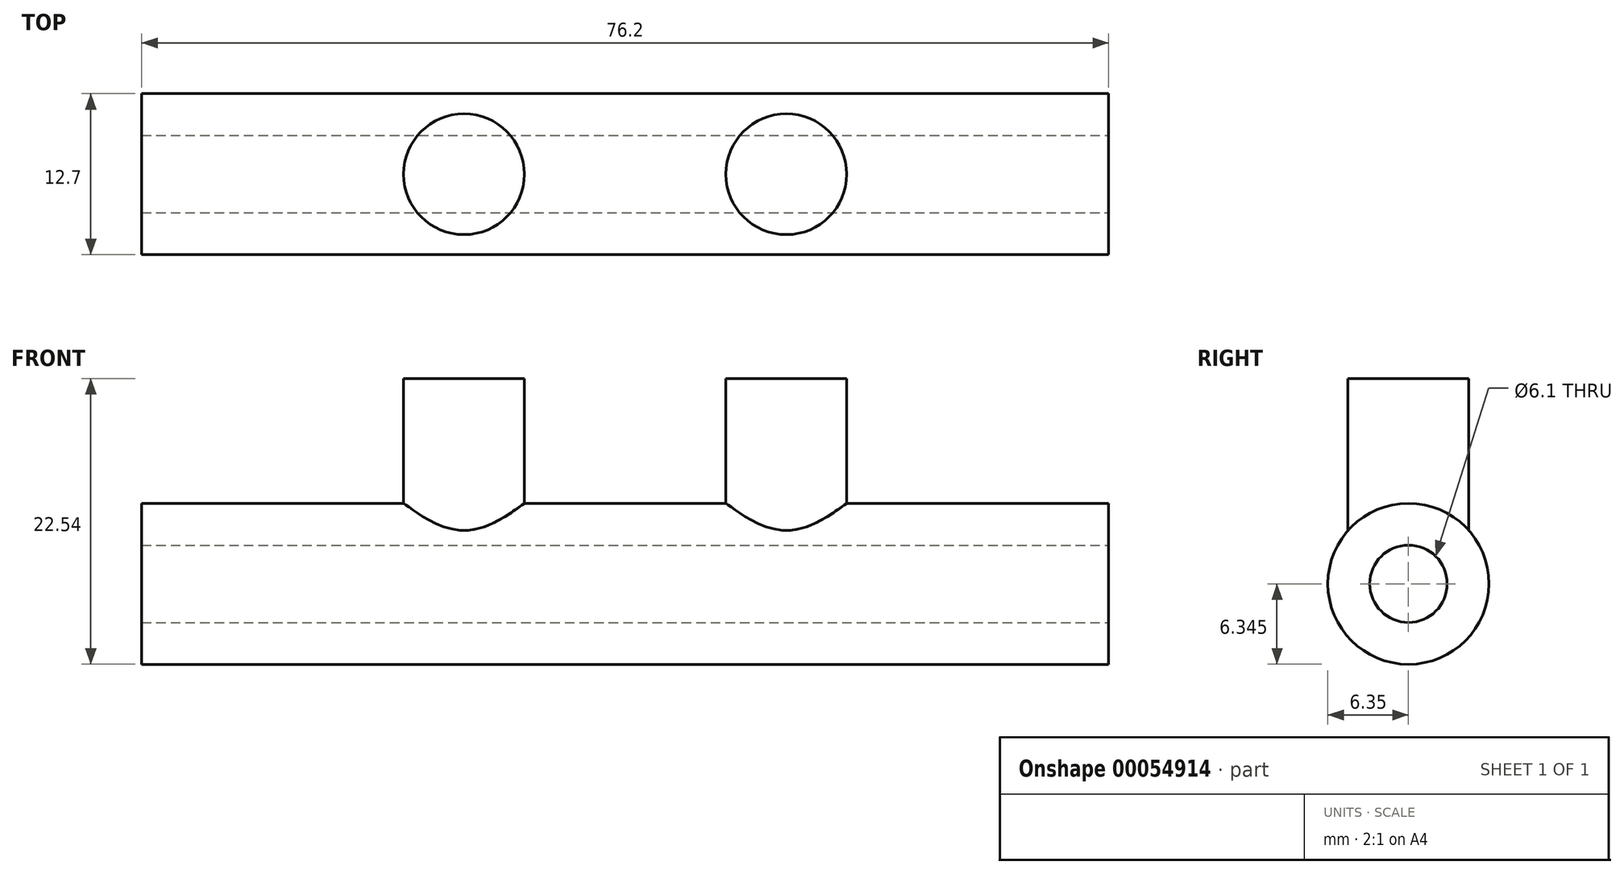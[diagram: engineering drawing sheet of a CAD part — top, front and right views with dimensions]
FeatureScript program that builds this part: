
annotation { "Feature Type Name" : "Feature", "Feature Type Description" : "" }
export const myFeature = defineFeature(function(context is Context, id is Id, definition is map)
    precondition{}
    {
        {
            var Q0;
            Q0=qCreatedBy(makeId("Right.planeOp"),FACE);
            var sketch = newSketch(context, id + "F0", { "sketchPlane" : qUnion([Q0])});
            skCircle(sketch, "E0", {"center": v(12.7, -6.66) * mm, "radius": 6.35 * mm});
            skPoint(sketch, "E1", {"position": v(12.7, -0.31) * mm});
            skSolve(sketch);
        }
        {
            var Q0;
            Q0=makeQuery(id+"F0.imprint","IMPRINT",FACE,{"disambiguationData":[TD([[makeQuery(id+"F0.imprint","IMPRINT",EDGE,{"derivedFrom":sQuery(id+"F0.wireOp",EDGE,"E0")}),1.0]])]});
            extrude(context, id + "F1", {"entities" : qUnion([Q0]), "oppositeDirection" : true, "depth" : 76.2 * mm});
        }
        {
            var Q0;
            Q0=makeQuery(id+"F1.opExtrude","CAP_FACE",FACE,{"disambiguationData":[OSD([sQuery(id+"F0.wireOp",EDGE,"E0")])],"isStart":true});
            var sketch = newSketch(context, id + "F2", { "sketchPlane" : qUnion([Q0])});
            skCircle(sketch, "E2", {"center": v(12.7, -6.66) * mm, "radius": 3.05 * mm});
            skSolve(sketch);
        }
        {
            var Q0;
            Q0 = qSketchRegion(id + "F2", true);
            var Q1;
            Q1=makeQuery(id+"F1.opExtrude","CAP_FACE",FACE,{"disambiguationData":[OSD([sQuery(id+"F0.wireOp",EDGE,"E0")])],"isStart":false});
            extrude(context, id + "F3", {"entities" : qUnion([Q0]), "operationType" : NewBodyOperationType.REMOVE, "endBound" : BoundingType.UP_TO_SURFACE, "oppositeDirection" : true, "endBoundEntityFace" : qUnion([Q1]), "depth" : 25.4 * mm});
        }
        {
            var Q0;
            Q0=qCreatedBy(makeId("Top.planeOp"),FACE);
            var sketch = newSketch(context, id + "F4", { "sketchPlane" : qUnion([Q0])});
            skCircle(sketch, "E3", {"center": v(-50.8, 12.7) * mm, "radius": 4.76 * mm});
            skCircle(sketch, "E4", {"center": v(-25.4, 12.7) * mm, "radius": 4.76 * mm});
            skLineSegment(sketch, "E5", {"start": v(-50.8, 12.7) * mm, "end": v(-25.4, 12.7) * mm, "construction": true});
            skPoint(sketch, "E6", {"position": v(-38.1, 12.7) * mm});
            skSolve(sketch);
        }
        {
            var Q0;
            Q0=makeQuery(id+"F4.imprint","IMPRINT",FACE,{"disambiguationData":[TD([[makeQuery(id+"F4.imprint","IMPRINT",EDGE,{"derivedFrom":sQuery(id+"F4.wireOp",EDGE,"E3")}),1.0]])]});
            var Q1;
            Q1=makeQuery(id+"F4.imprint","IMPRINT",FACE,{"disambiguationData":[TD([[makeQuery(id+"F4.imprint","IMPRINT",EDGE,{"derivedFrom":sQuery(id+"F4.wireOp",EDGE,"E4")}),1.0]])]});
            extrude(context, id + "F5", {"entities" : qUnion([Q0, Q1]), "operationType" : NewBodyOperationType.ADD, "depth" : 9.52 * mm, "hasSecondDirection" : true, "secondDirectionOppositeDirection" : true, "secondDirectionDepth" : 2.54 * mm});
        }
    });
